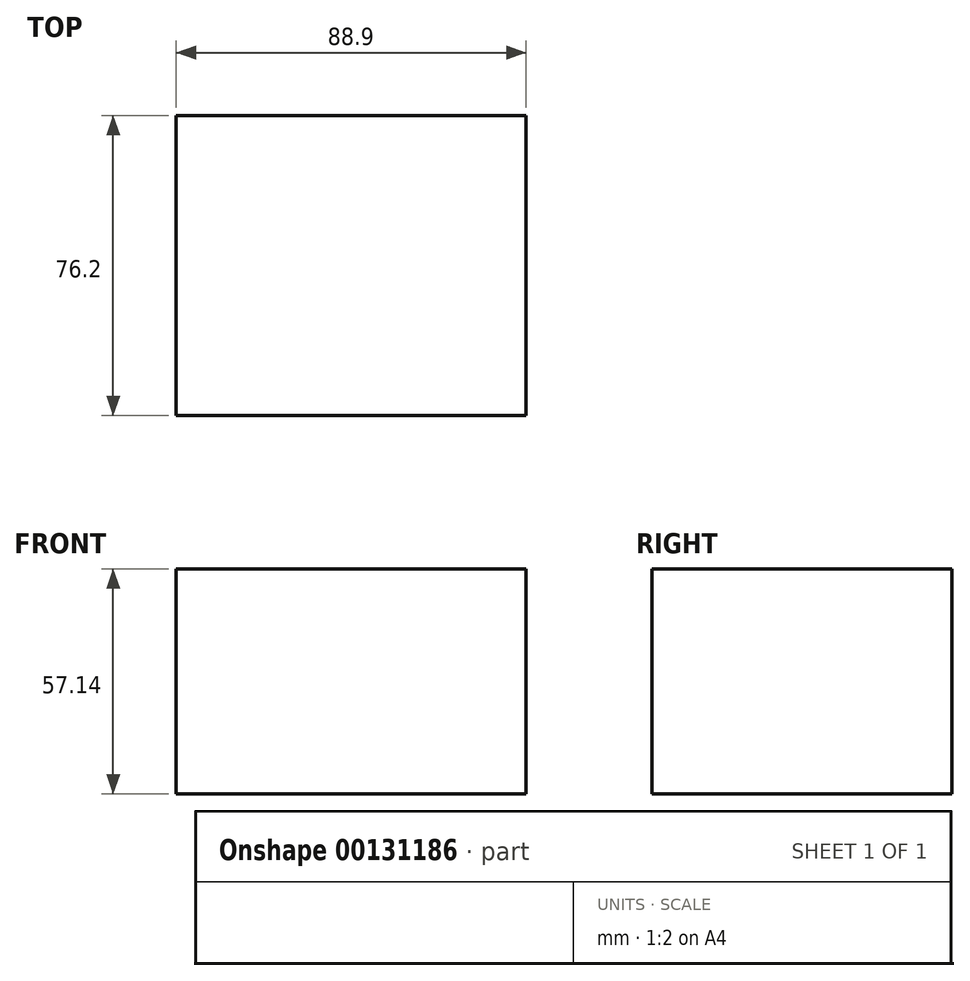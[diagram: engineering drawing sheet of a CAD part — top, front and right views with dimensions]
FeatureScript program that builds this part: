
annotation { "Feature Type Name" : "Feature", "Feature Type Description" : "" }
export const myFeature = defineFeature(function(context is Context, id is Id, definition is map)
    precondition{}
    {
        {
            var Q0;
            Q0=qCreatedBy(makeId("Front.planeOp"),FACE);
            var sketch = newSketch(context, id + "F0", { "sketchPlane" : qUnion([Q0])});
            skLineSegment(sketch, "E0.bottom", {"start": v(44.45, -28.57) * mm, "end": v(-44.45, -28.58) * mm});
            skLineSegment(sketch, "E0.top", {"start": v(44.45, 28.58) * mm, "end": v(-44.45, 28.57) * mm});
            skLineSegment(sketch, "E0.left", {"start": v(44.45, -28.58) * mm, "end": v(44.45, 28.58) * mm});
            skLineSegment(sketch, "E0.right", {"start": v(-44.45, -28.58) * mm, "end": v(-44.45, 28.58) * mm});
            skPoint(sketch, "E0.middle", {"position": v(0, 0) * mm});
            skSolve(sketch);
        }
        {
            var Q0;
            Q0=makeQuery(id+"F0.imprint","IMPRINT",FACE,{"disambiguationData":[TD([[makeQuery(id+"F0.imprint","IMPRINT",EDGE,{"derivedFrom":sQuery(id+"F0.wireOp",EDGE,"E0.bottom")}),-1.0]])]});
            extrude(context, id + "F1", {"entities" : qUnion([Q0]), "endBound" : BoundingType.SYMMETRIC, "depth" : 76.2 * mm});
        }
    });
